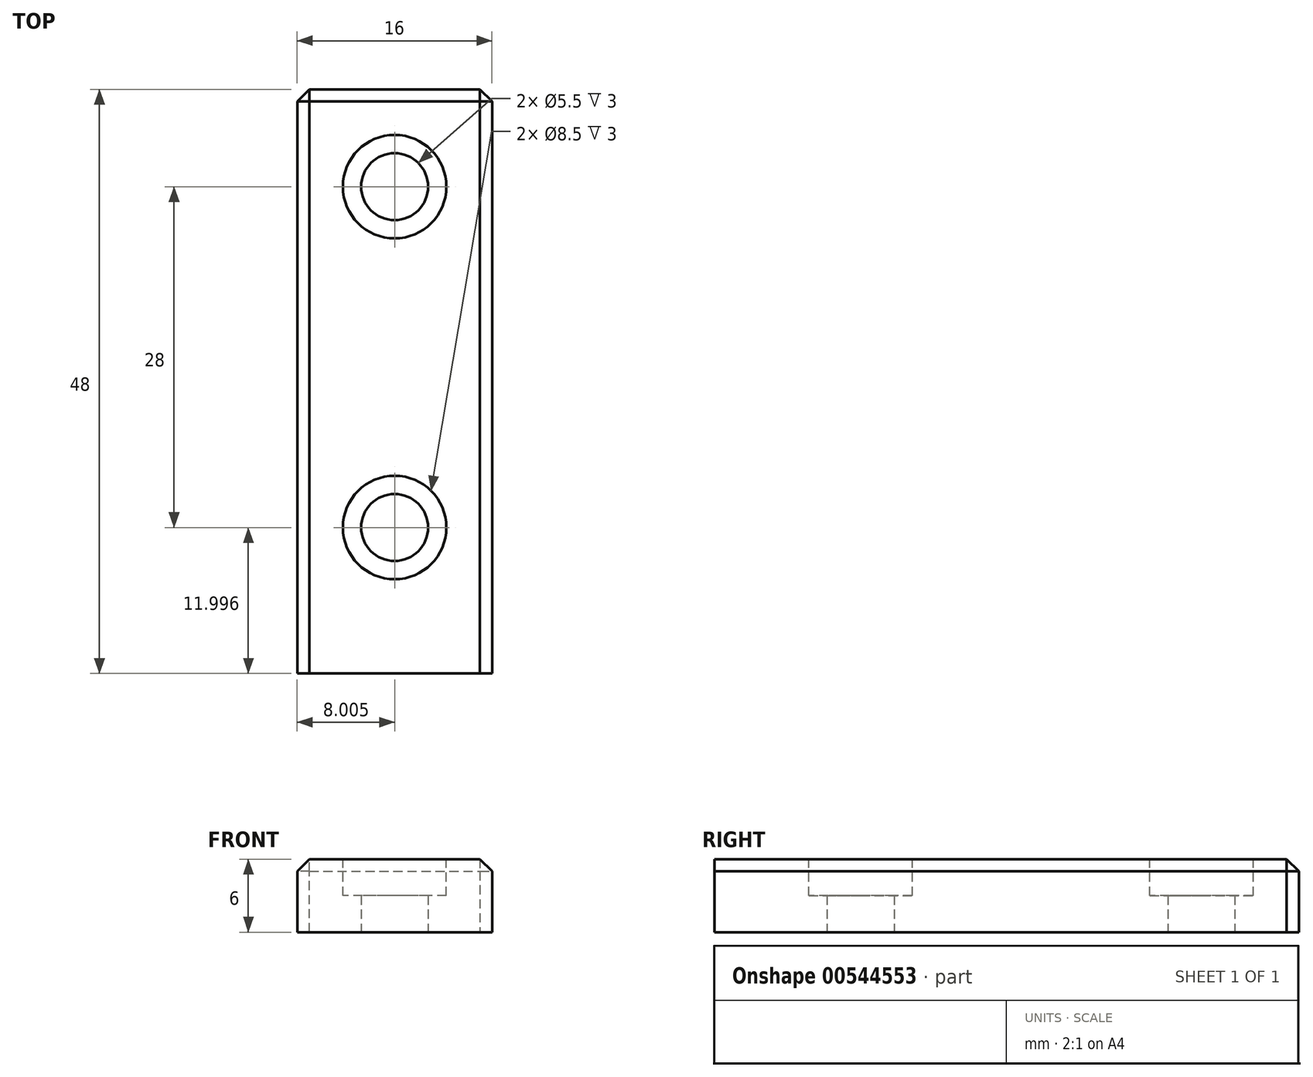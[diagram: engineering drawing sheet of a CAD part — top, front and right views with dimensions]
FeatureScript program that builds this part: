
annotation { "Feature Type Name" : "Feature", "Feature Type Description" : "" }
export const myFeature = defineFeature(function(context is Context, id is Id, definition is map)
    precondition{}
    {
        {
            var Q0;
            Q0=qCreatedBy(makeId("Top.planeOp"),FACE);
            var sketch = newSketch(context, id + "F0", { "sketchPlane" : qUnion([Q0])});
            skLineSegment(sketch, "E0.bottom", {"start": v(-29.77, 31.99) * mm, "end": v(-13.77, 31.99) * mm});
            skLineSegment(sketch, "E0.top", {"start": v(-29.77, -16.01) * mm, "end": v(-13.77, -16.01) * mm});
            skLineSegment(sketch, "E0.left", {"start": v(-29.77, 31.99) * mm, "end": v(-29.77, -16.01) * mm});
            skLineSegment(sketch, "E0.right", {"start": v(-13.77, 31.99) * mm, "end": v(-13.77, -16.01) * mm});
            skCircle(sketch, "E1", {"center": v(-21.77, -4.01) * mm, "radius": 2.75 * mm});
            skCircle(sketch, "E2", {"center": v(-21.77, 23.99) * mm, "radius": 2.75 * mm});
            skPoint(sketch, "E3", {"position": v(-21.77, -16.01) * mm});
            skSolve(sketch);
        }
        {
            var Q0;
            Q0=makeQuery(id+"F0.imprint","IMPRINT",FACE,{"disambiguationData":[TD([[makeQuery(id+"F0.imprint","IMPRINT",EDGE,{"derivedFrom":sQuery(id+"F0.wireOp",EDGE,"E0.bottom")}),-1.0]])]});
            extrude(context, id + "F1", {"entities" : qUnion([Q0]), "depth" : 6 * mm, "offsetDistance" : 25 * mm});
        }
        {
            var Q0;
            Q0=makeQuery(id+"F1.opExtrude","CAP_FACE",FACE,{"disambiguationData":[OSD([sQuery(id+"F0.wireOp",EDGE,"E0.bottom"),sQuery(id+"F0.wireOp",EDGE,"E0.top"),sQuery(id+"F0.wireOp",EDGE,"E0.left"),sQuery(id+"F0.wireOp",EDGE,"E0.right"),sQuery(id+"F0.wireOp",EDGE,"E1"),sQuery(id+"F0.wireOp",EDGE,"E2")])],"isStart":false});
            var sketch = newSketch(context, id + "F2", { "sketchPlane" : qUnion([Q0])});
            skCircle(sketch, "E4", {"center": v(-21.77, 23.99) * mm, "radius": 4.25 * mm});
            skCircle(sketch, "E5", {"center": v(-21.77, -4.01) * mm, "radius": 4.25 * mm});
            skSolve(sketch);
        }
        {
            var Q0;
            Q0 = qSketchRegion(id + "F2", true);
            extrude(context, id + "F3", {"entities" : qUnion([Q0]), "operationType" : NewBodyOperationType.REMOVE, "oppositeDirection" : true, "depth" : 3 * mm, "offsetDistance" : 25 * mm});
        }
        {
            var Q0;
            Q0=makeQuery(id+"F1.opExtrude","SWEPT_EDGE",EDGE,{"disambiguationData":[OSD([sQuery(id+"F0.wireOp",EDGE,"E0.bottom"),sQuery(id+"F0.wireOp",EDGE,"E0.left")])]});
            var Q1;
            Q1=makeQuery(id+"F1.opExtrude","CAP_EDGE",EDGE,{"disambiguationData":[OSD([sQuery(id+"F0.wireOp",EDGE,"E0.bottom")])],"isStart":false});
            var Q2;
            Q2=makeQuery(id+"F1.opExtrude","SWEPT_EDGE",EDGE,{"disambiguationData":[OSD([sQuery(id+"F0.wireOp",EDGE,"E0.bottom"),sQuery(id+"F0.wireOp",EDGE,"E0.right")])]});
            var Q3;
            Q3=makeQuery(id+"F1.opExtrude","CAP_EDGE",EDGE,{"disambiguationData":[OSD([sQuery(id+"F0.wireOp",EDGE,"E0.left")])],"isStart":false});
            var Q4;
            Q4=makeQuery(id+"F1.opExtrude","CAP_EDGE",EDGE,{"disambiguationData":[OSD([sQuery(id+"F0.wireOp",EDGE,"E0.right")])],"isStart":false});
            chamfer(context, id + "F4", {"entities" : qUnion([Q0, Q1, Q2, Q3, Q4]), "width" : 1 * mm, "tangentPropagation" : true});
        }
    });
